# Revit family: Electronics_Commercial-Audio_Biamp_Tabletop-Cable-Management_1-power-connection
name_source: partatom
category: Communication Devices
units: mm (PartAtom-declared; Revit-internal decimal feet)

## family parameters
Cut with Voids When Loaded = No
Host = Face
Maintain Annotation Orientation = No
OmniClass Number = 23.85.10.17.11
Part Type = Normal
Room Calculation Point = No
Round Connector Dimension = Use Diameter
Shared = No

## types (4) — shared parameters
Altitude = 0-6,600 ft (0-2000m) MSL
Apparent Load = 0 VA
Compliace = CE Marked (Europe), RoHS Directive (Europe)
Configurable = supports one power connection and one control pad
Connector Description = Power connector
Default Elevation = 4' - 0"
Depth = 0' - 5 1/2"
Description = EasyConnect Tabletop Cable Management and Control Solution
Height = 0' - 4"
Housing Material = Biamp - Plastic - Black
Humidity = 10-90% relative humidity (non-condensing)
Included cables = HDMI, VGA, 3.5 mm audio, USB-A, 2X CAT5
Manufacturer = Biamp
Max Power Consumption = 0 W
Number of Poles = 1
Overall Depth = 0' - 3 1/2"
Overall Width = 0' - 8 1/2"
Power Factor = 1
Product Documentation Link = https://downloads.biamp.com
Product Page URL = https://www.biamp.com
Product data url = https://www.bimobject.com
Supports the following control pads = Impera Sierra II, Impera Echo, Impera Echo Plus and Impera Oscar
Temperature Range = 32 - 86° F (0 – 30° C)
URL = https://www.biamp.com
Voltage = 120 V
Weight = 5.50 lbf
Width = 0' - 10"

## per-type parameters (varying)
| type | EC-PKP-CH | EC-PKP-DK | EC-PKP-EU |
| EC-PKP-EU | No | No | Yes |
| EC-PKP-DK | No | Yes | No |
| EC-PKP-UNI | No | No | No |
| EC-PKP-CH | Yes | No | No |

note: column(s) folded — value = type name in every type: Model

type visibility flags (boolean, named after types; folded from table):
- EC-PKP-EU: Yes: (none)
- EC-PKP-DK: Yes: (none)
- EC-PKP-UNI: Yes: EC-PKP-UNI
- EC-PKP-CH: Yes: (none)

## geometry (parser evidence)
native form markers: Sweep x8
no freeform markers — native parametric forms only
